# Revit family: Outdoor-Kitchen-Cabinets_Kalamazoo_Appliance-Surrounds_Arcadia
name_source: partatom
category: Specialty Equipment
revit_build: Autodesk Revit 2018 (Build: 20190510_1515(x64)
units: mm (PartAtom-declared; Revit-internal decimal feet)

## family parameters
Always vertical = Yes
Cut with Voids When Loaded = No
OmniClass Number = 23.40.40.11
OmniClass Title = Specialized Food Storage and Display Furnishings
Part Type = Normal
Room Calculation Point = No
Round Connector Dimension = Use Diameter
Shared = No
Work Plane-Based = No

## types (8) — shared parameters
Assembly Code = E1090300
Depth = 29 1/8"
Keynote = 11400
Manufacturer = Kalamazoo Outdoor Gourmet
Product Material = Kalamazoo - Stainless Steel - 304 OR 316L
Product data url = https://www.bimobject.com
URL = https://kalamazoogourmet.com
Ι_Gnrc Mdl Optn 01 = Extension : +3/4"
Ι_Gnrc Mdl Optn 02 = Extension : -3/4"

## per-type parameters (varying)
| type | Description | L | R | Weight (lb) | Width |
| KD-ANC-21-EL | Arcadia 15-Inch Appliance Cabinet | Yes | No | 190.00 lbf | 21" |
| KD-ANC-30-ER | Arcadia 24-Inch Appliance Cabinet | No | Yes | 210.00 lbf | 30" |
| KD-ANC-45-EL | Arcadia 39-Inch Appliance Cabinet | Yes | No | 250.00 lbf | 45" |
| KD-ANC-54-EL | Arcadia 48-Inch Appliance Cabinet | Yes | No | 275.00 lbf | 54" |
| KD-ANC-21-ER | Arcadia 15-Inch Appliance Cabinet | No | Yes | 190.00 lbf | 21" |
| KD-ANC-45-ER | Arcadia 39-Inch Appliance Cabinet | No | Yes | 250.00 lbf | 45" |
| KD-ANC-30-EL | Arcadia 24-Inch Appliance Cabinet | Yes | No | 210.00 lbf | 30" |
| KD-ANC-54-ER | Arcadia 48-Inch Appliance Cabinet | No | Yes | 275.00 lbf | 54" |

note: column(s) folded — value = type name in every type: Model

## geometry (parser evidence)
native form markers: Sweep x5
no freeform markers — native parametric forms only
